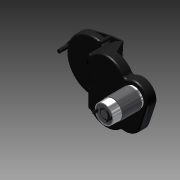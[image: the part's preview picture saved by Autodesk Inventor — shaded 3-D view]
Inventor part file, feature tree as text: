
AUTODESK INVENTOR PART (.ipt)
format: ipt  version: 2011 (Build 150239000, 239)  size: 315,392 bytes
history: native  units: mm (DEFAULTED — no unit token found)
features: sketch x13, extrude x12, fillet x7, plane x3, other x1, chamfer x1, pattern_circular x1
ambient origin geometry x8: Origin, YZ Plane, XZ Plane, XY Plane, X Axis, Y Axis, Z Axis, Center Point
bodies: Solid1 (feature_tree)
feature tree (38):
  extrude  "Extrusion1"  Depth=76.2mm
  fillet  "Fillet1"  Radius=43.18mm
  extrude  "Extrusion2"  Depth=53.848mm
  fillet  "Fillet2"  Radius=50.8mm
  fillet  "Fillet3"  Radius=3.048mm
  fillet  "Fillet4"  Radius=66.04mm
  fillet  "Fillet5"  Radius=34.29mm
  extrude  "Extrusion8"  Depth=41.91mm TaperAngle=0.0deg
  extrude  "Extrusion9"  Depth=28.448mm TaperAngle=0.0deg
  fillet  "Fillet9"  Radius=6.35mm
  extrude  "Extrusion10"  Depth=3.175mm
  other  "Work Axis1"
  sketch  "Sketch12"  dims[d19=3.175mm d22=15.24mm]
  plane  "Work Plane1"
  extrude  "Extrusion11"  Depth=15.24mm
  extrude  "Extrusion14"  Depth=78.3082mm
  extrude  "Extrusion15"  Depth=2.54mm TaperAngle=0.0deg
  plane  "Work Plane2"
  plane  "Work Plane3"
  extrude  "Extrusion16"  Depth=3.81mm
  fillet  "Fillet10"  Radius=7.62mm
  extrude  "Extrusion17"  Depth=25.4mm
  extrude  "Extrusion18"  Depth=25.4mm
  chamfer  "Chamfer1"  Distance=17.78mm
  pattern_circular  "Circular Pattern1"  [2 undecoded]
  sketch  "Sketch1"  dims[d0=99.06mm d1=76.2mm d2=43.18mm]
  sketch  "Sketch2"  dims[d3=53.848mm d4=53.848mm d5=50.8mm d7=3.048mm d8=66.04mm d9=34.29mm]
  sketch  "Sketch9"  dims[d10=19.05mm d11=41.91mm d12=0.0mm]
  sketch  "Sketch10"  dims[d13=6.35mm d14=28.448mm d15=0.0mm d16=6.35mm]
  sketch  "Sketch11"  dims[d17=3.175mm d18=3.175mm]
  sketch  "Sketch13"  dims[d43=8.89mm d44=78.3082mm]
  sketch  "Sketch15"  dims[d45=2.54mm d46=0.0mm d47=2.54mm d48=0.0mm]
  sketch  "Sketch16"  dims[d49=3.175mm d50=3.81mm d51=7.62mm]
  sketch  "Sketch17"  dims[d52=17.78mm d53=-0.349066mm d55=25.4mm]
  sketch  "Sketch18"  dims[d56=38.1mm d57=25.4mm d58=17.78mm d59=0.0mm]
  sketch  "Sketch19"  dims[d65=0.0mm d66=5.588mm]
  sketch  "Sketch20"  dims[d67=6.35mm d68=13.462mm d69=35.56mm d70=57.15mm d71=0.0mm d72=1.27mm d73=0.0mm d74=-16.002mm d75=-36.83mm d76=1.27mm d77=-1.047198mm d78=1.524mm d79=38.1mm d80=1.27mm d81=0.0mm d82=10.16mm d83=0.0mm d84=1.524mm d85=1.524mm d86=20.0mm d88=360.0deg d89=45.0deg]
  extrude  "Extrusion13"  Depth=57.15mm TaperAngle=0.0deg
note: 2 required parameter values undecoded (feature->parameter linkage not recoverable at this tier; creation-order binding heuristic only, values carry confidence <= 0.55)
